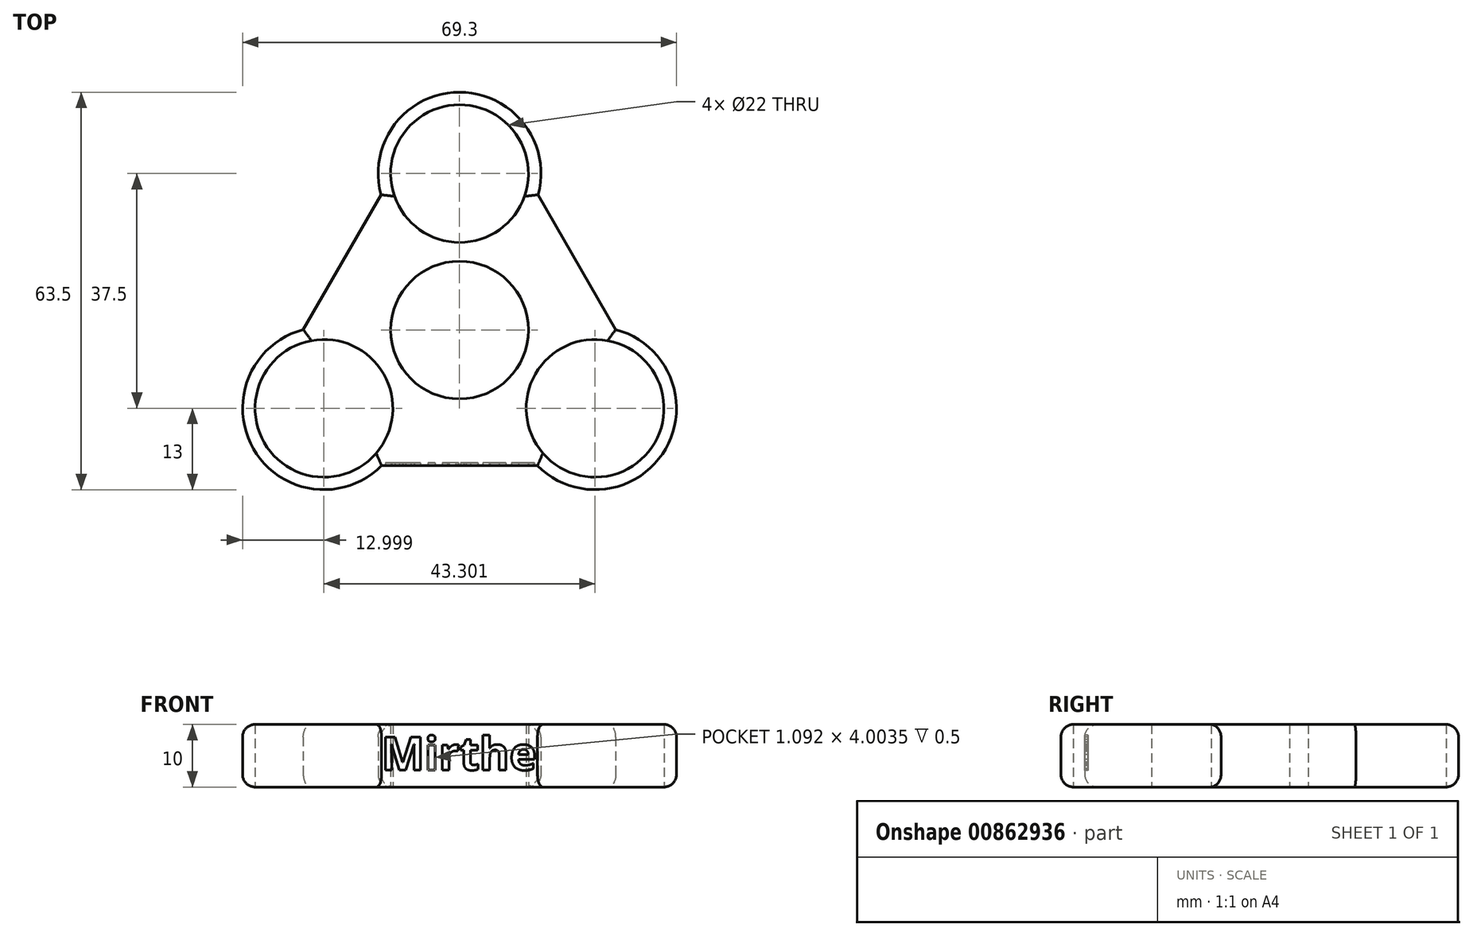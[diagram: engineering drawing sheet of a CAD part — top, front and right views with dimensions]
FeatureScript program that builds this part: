
annotation { "Feature Type Name" : "Feature", "Feature Type Description" : "" }
export const myFeature = defineFeature(function(context is Context, id is Id, definition is map)
    precondition{}
    {
        {
            var Q0;
            Q0=qCreatedBy(makeId("Top.planeOp"),FACE);
            var sketch = newSketch(context, id + "F0", { "sketchPlane" : qUnion([Q0])});
            skCircle(sketch, "E0", {"center": v(0, 0) * mm, "radius": 11 * mm});
            skArc(sketch, "E1", {"start": v(0, 25) * mm, "mid": v(-17.68, -17.68) * mm, "end": v(25, 0) * mm, "construction": true});
            skArc(sketch, "E2.cCircle", {"start": v(21.65, -12.5) * mm, "mid": v(21.65, 12.5) * mm, "end": v(0, 25) * mm, "construction": true});
            skLineSegment(sketch, "E2.0", {"start": v(0, 25) * mm, "end": v(21.65, -12.5) * mm, "construction": true});
            skLineSegment(sketch, "E2.1", {"start": v(21.65, -12.5) * mm, "end": v(-21.65, -12.5) * mm, "construction": true});
            skLineSegment(sketch, "E2.2", {"start": v(-21.65, -12.5) * mm, "end": v(0, 25) * mm, "construction": true});
            skCircle(sketch, "E3", {"center": v(-21.65, -12.5) * mm, "radius": 11 * mm});
            skCircle(sketch, "E4", {"center": v(21.65, -12.5) * mm, "radius": 11 * mm});
            skCircle(sketch, "E5", {"center": v(0, 25) * mm, "radius": 11 * mm});
            skCircle(sketch, "E6", {"center": v(0, 25) * mm, "radius": 13 * mm});
            skCircle(sketch, "E7", {"center": v(-21.65, -12.5) * mm, "radius": 13 * mm});
            skCircle(sketch, "E8", {"center": v(21.65, -12.5) * mm, "radius": 13 * mm});
            skLineSegment(sketch, "E9", {"start": v(-12.55, 21.62) * mm, "end": v(-25, 0) * mm});
            skLineSegment(sketch, "E10", {"start": v(-12.45, -21.68) * mm, "end": v(12.45, -21.68) * mm});
            skLineSegment(sketch, "E11", {"start": v(12.55, 21.62) * mm, "end": v(25, 0) * mm});
            skSolve(sketch);
        }
        {
            var Q0;
            Q0=makeQuery(id+"F0.imprint","IMPRINT",FACE,{"disambiguationData":[TD([[makeQuery(id+"F0.imprint","IMPRINT",EDGE,{"derivedFrom":sQuery(id+"F0.wireOp",EDGE,"E3")}),-1.0]])]});
            var Q1;
            Q1=makeQuery(id+"F0.imprint","IMPRINT",FACE,{"disambiguationData":[TD([[makeQuery(id+"F0.imprint","IMPRINT",EDGE,{"derivedFrom":sQuery(id+"F0.wireOp",EDGE,"E0")}),-1.0]])]});
            var Q2;
            Q2=makeQuery(id+"F0.imprint","IMPRINT",FACE,{"disambiguationData":[TD([[makeQuery(id+"F0.imprint","IMPRINT",EDGE,{"derivedFrom":sQuery(id+"F0.wireOp",EDGE,"E4")}),-1.0]])]});
            var Q3;
            Q3=makeQuery(id+"F0.imprint","IMPRINT",FACE,{"disambiguationData":[TD([[makeQuery(id+"F0.imprint","IMPRINT",EDGE,{"derivedFrom":sQuery(id+"F0.wireOp",EDGE,"E5")}),-1.0]])]});
            extrude(context, id + "F1", {"entities" : qUnion([Q0, Q1, Q2, Q3]), "depth" : 10 * mm, "offsetDistance" : 25 * mm});
        }
        {
            var Q0;
            Q0=makeQuery(id+"F1.opExtrude","CAP_EDGE",EDGE,{"disambiguationData":[OSD([sQuery(id+"F0.wireOp",EDGE,"E7")])],"isStart":false});
            var Q1;
            Q1=makeQuery(id+"F1.opExtrude","CAP_EDGE",EDGE,{"disambiguationData":[OSD([sQuery(id+"F0.wireOp",EDGE,"E9")])],"isStart":false});
            var Q2;
            Q2=makeQuery(id+"F1.opExtrude","CAP_EDGE",EDGE,{"disambiguationData":[OSD([sQuery(id+"F0.wireOp",EDGE,"E6")])],"isStart":false});
            var Q3;
            Q3=makeQuery(id+"F1.opExtrude","CAP_EDGE",EDGE,{"disambiguationData":[OSD([sQuery(id+"F0.wireOp",EDGE,"E11")])],"isStart":false});
            var Q4;
            Q4=makeQuery(id+"F1.opExtrude","CAP_EDGE",EDGE,{"disambiguationData":[OSD([sQuery(id+"F0.wireOp",EDGE,"E8")])],"isStart":false});
            var Q5;
            Q5=makeQuery(id+"F1.opExtrude","CAP_EDGE",EDGE,{"disambiguationData":[OSD([sQuery(id+"F0.wireOp",EDGE,"E10")])],"isStart":false});
            var Q6;
            Q6=makeQuery(id+"F1.opExtrude","CAP_EDGE",EDGE,{"disambiguationData":[OSD([sQuery(id+"F0.wireOp",EDGE,"E10")])],"isStart":true});
            var Q7;
            Q7=makeQuery(id+"F1.opExtrude","CAP_EDGE",EDGE,{"disambiguationData":[OSD([sQuery(id+"F0.wireOp",EDGE,"E7")])],"isStart":true});
            var Q8;
            Q8=makeQuery(id+"F1.opExtrude","CAP_EDGE",EDGE,{"disambiguationData":[OSD([sQuery(id+"F0.wireOp",EDGE,"E9")])],"isStart":true});
            var Q9;
            Q9=makeQuery(id+"F1.opExtrude","CAP_EDGE",EDGE,{"disambiguationData":[OSD([sQuery(id+"F0.wireOp",EDGE,"E6")])],"isStart":true});
            var Q10;
            Q10=makeQuery(id+"F1.opExtrude","CAP_EDGE",EDGE,{"disambiguationData":[OSD([sQuery(id+"F0.wireOp",EDGE,"E11")])],"isStart":true});
            var Q11;
            Q11=makeQuery(id+"F1.opExtrude","CAP_EDGE",EDGE,{"disambiguationData":[OSD([sQuery(id+"F0.wireOp",EDGE,"E8")])],"isStart":true});
            fillet(context, id + "F2", {"entities" : qUnion([Q0, Q1, Q2, Q3, Q4, Q5, Q6, Q7, Q8, Q9, Q10, Q11]), "radius" : 2 * mm, "tangentPropagation" : true, "allowEdgeOverflow" : false});
        }
        {
            var Q0;
            Q0=makeQuery(id+"F1.opExtrude","SWEPT_FACE",FACE,{"disambiguationData":[OSD([sQuery(id+"F0.wireOp",EDGE,"E10")])]});
            var sketch = newSketch(context, id + "F3", { "sketchPlane" : qUnion([Q0])});
            skText(sketch, "E12", { "text": "Mirthe", "fontName": "OpenSans-Bold.ttf"});
            const initialGuessF3  = {"E12": [-0.0125, 0.00272, 1, 0, 0.00528]};
            skSetInitialGuess(sketch, initialGuessF3);
            skSolve(sketch);
        }
        {
            var Q0;
            Q0 = qSketchRegion(id + "F3", true);
            extrude(context, id + "F4", {"entities" : qUnion([Q0]), "operationType" : NewBodyOperationType.REMOVE, "oppositeDirection" : true, "depth" : 0.5 * mm, "offsetDistance" : 25 * mm});
        }
    });
